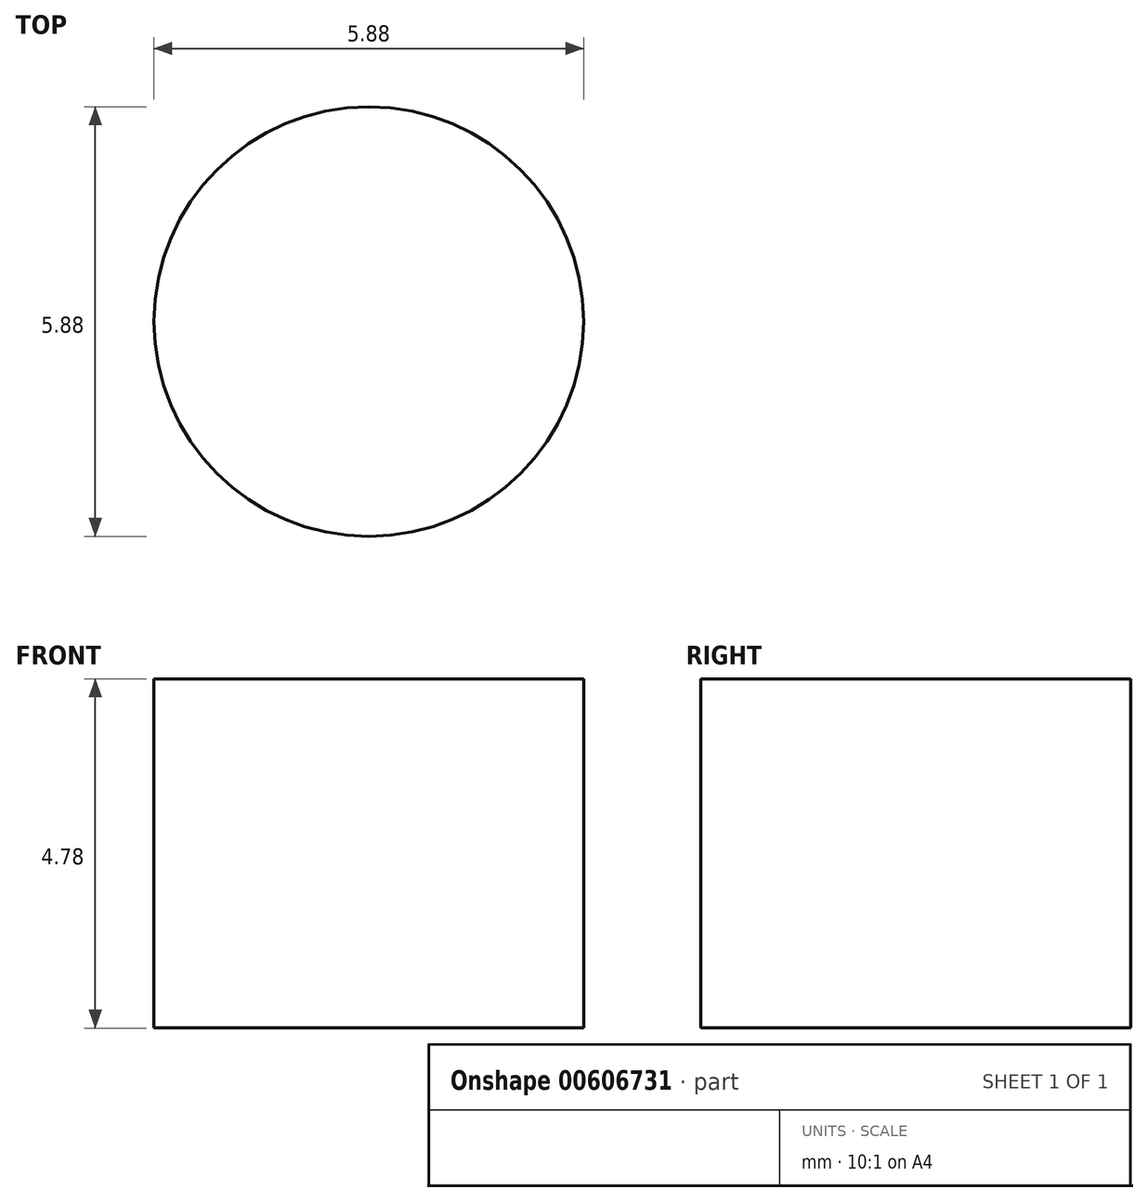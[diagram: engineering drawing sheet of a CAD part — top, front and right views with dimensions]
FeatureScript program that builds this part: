
annotation { "Feature Type Name" : "Feature", "Feature Type Description" : "" }
export const myFeature = defineFeature(function(context is Context, id is Id, definition is map)
    precondition{}
    {
        {
            var Q0;
            Q0=qCreatedBy(makeId("Top.planeOp"),FACE);
            var sketch = newSketch(context, id + "F0", { "sketchPlane" : qUnion([Q0])});
            skCircle(sketch, "E0", {"center": v(0, 0) * mm, "radius": 1.62 * mm});
            skCircle(sketch, "E1", {"center": v(0, 0) * mm, "radius": 2.03 * mm});
            skSolve(sketch);
        }
        {
            var Q0;
            Q0=makeQuery(id+"F0.imprint","IMPRINT",FACE,{"disambiguationData":[TD([[makeQuery(id+"F0.imprint","IMPRINT",EDGE,{"derivedFrom":sQuery(id+"F0.wireOp",EDGE,"E0")}),-1.0]])]});
            extrude(context, id + "F1", {"entities" : qUnion([Q0]), "oppositeDirection" : true, "depth" : 1.27 * mm, "offsetDistance" : 25.4 * mm});
        }
        {
            var Q0;
            Q0=makeQuery(id+"F1.opExtrude","CAP_FACE",FACE,{"disambiguationData":[OSD([sQuery(id+"F0.wireOp",EDGE,"E0"),sQuery(id+"F0.wireOp",EDGE,"E1")])],"isStart":true});
            var sketch = newSketch(context, id + "F2", { "sketchPlane" : qUnion([Q0])});
            skCircle(sketch, "E2", {"center": v(0, 0) * mm, "radius": 2.94 * mm});
            skSolve(sketch);
        }
        {
            var Q0;
            Q0 = qSketchRegion(id + "F2", true);
            extrude(context, id + "F3", {"entities" : qUnion([Q0]), "operationType" : NewBodyOperationType.ADD, "oppositeDirection" : true, "depth" : 4.78 * mm, "offsetDistance" : 25.4 * mm});
        }
    });
